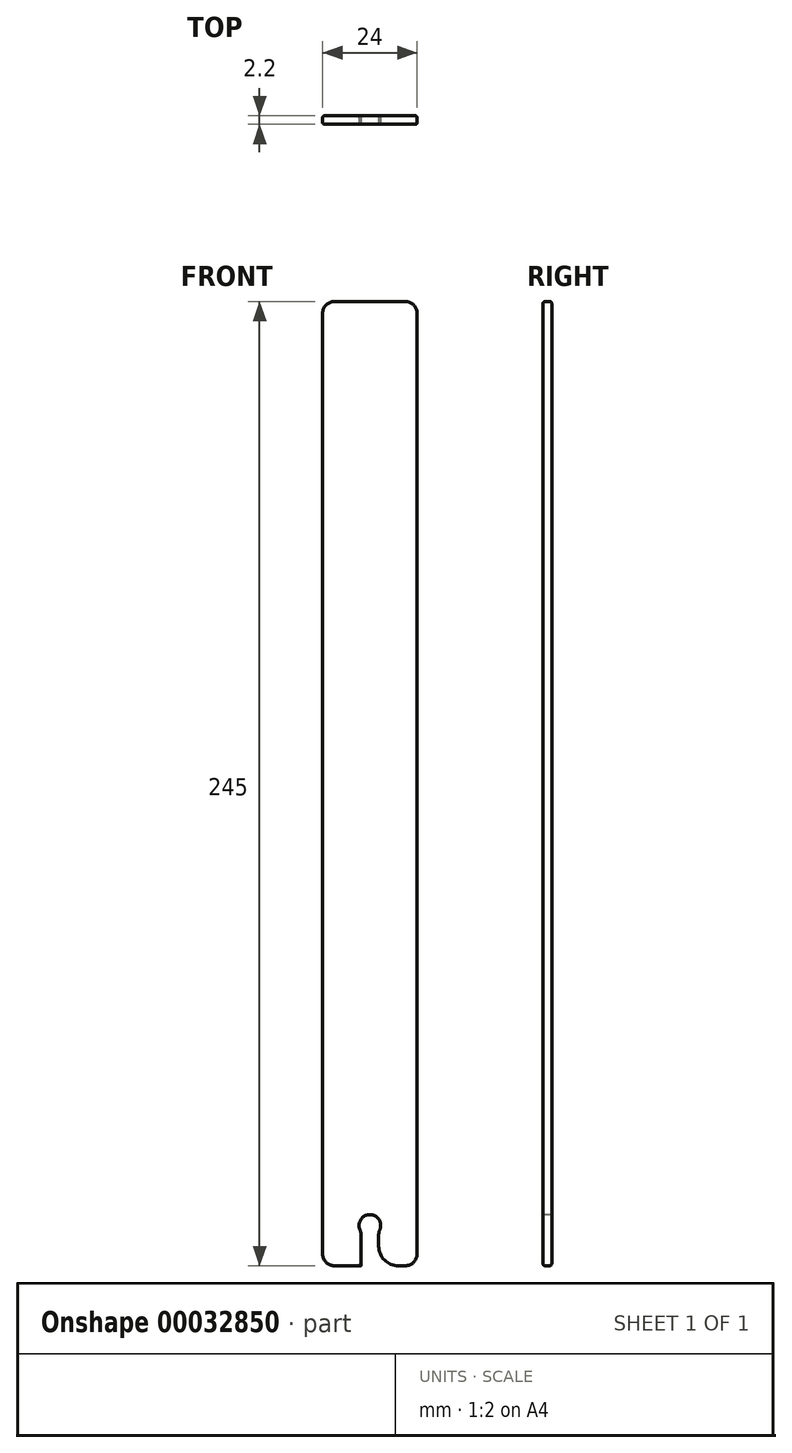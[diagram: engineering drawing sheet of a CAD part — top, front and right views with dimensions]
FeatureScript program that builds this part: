
annotation { "Feature Type Name" : "Feature", "Feature Type Description" : "" }
export const myFeature = defineFeature(function(context is Context, id is Id, definition is map)
    precondition{}
    {
        {
            var Q0;
            Q0=qCreatedBy(makeId("Top.planeOp"),FACE);
            var sketch = newSketch(context, id + "F0", { "sketchPlane" : qUnion([Q0])});
            skLineSegment(sketch, "E0.rect.bottom", {"start": v(12, 1.1) * mm, "end": v(-12, 1.1) * mm});
            skLineSegment(sketch, "E0.rect.top", {"start": v(12, -1.1) * mm, "end": v(-12, -1.1) * mm});
            skLineSegment(sketch, "E0.rect.left", {"start": v(12, 1.1) * mm, "end": v(12, -1.1) * mm});
            skLineSegment(sketch, "E0.rect.right", {"start": v(-12, 1.1) * mm, "end": v(-12, -1.1) * mm});
            skPoint(sketch, "E0.rect.middle", {"position": v(0, 0) * mm});
            skSolve(sketch);
        }
        {
            var Q0;
            Q0 = qSketchRegion(id + "F0", true);
            extrude(context, id + "F1", {"entities" : qUnion([Q0]), "depth" : 245 * mm});
        }
        {
            var Q0;
            Q0=qCreatedBy(makeId("Front.planeOp"),FACE);
            var sketch = newSketch(context, id + "F2", { "sketchPlane" : qUnion([Q0])});
            skArc(sketch, "E1", {"start": v(2.25, 8.67) * mm, "mid": v(0, 13) * mm, "end": v(-2.25, 8.67) * mm});
            skLineSegment(sketch, "E2", {"start": v(-2.25, 8.67) * mm, "end": v(-2.25, 0) * mm});
            skLineSegment(sketch, "E3.MirrorCS", {"start": v(2.25, 8.67) * mm, "end": v(2.25, 0) * mm});
            skPoint(sketch, "E4", {"position": v(0, 13) * mm});
            skLineSegment(sketch, "E5", {"start": v(-2.25, 0) * mm, "end": v(2.25, 0) * mm});
            skSolve(sketch);
        }
        {
            var Q0;
            Q0 = qSketchRegion(id + "F2", true);
            extrude(context, id + "F3", {"entities" : qUnion([Q0]), "operationType" : NewBodyOperationType.REMOVE, "endBound" : BoundingType.THROUGH_ALL, "oppositeDirection" : true, "depth" : 25 * mm, "hasSecondDirection" : true, "secondDirectionBound" : SecondDirectionBoundingType.THROUGH_ALL, "secondDirectionOppositeDirection" : false, "secondDirectionDepth" : 25 * mm});
        }
        {
            var Q0;
            Q0=makeQuery(id+"F3.boolean.opBoolean","COPY",EDGE,{"derivedFrom":makeQuery(id+"F3.opExtrude","SWEPT_EDGE",EDGE,{"disambiguationData":[OSD([sQuery(id+"F2.wireOp",EDGE,"E3.MirrorCS"),sQuery(id+"F2.wireOp",EDGE,"E5")])]})});
            var Q1;
            Q1=makeQuery(id+"F3.boolean.opBoolean","COPY",EDGE,{"derivedFrom":makeQuery(id+"F3.opExtrude","SWEPT_EDGE",EDGE,{"disambiguationData":[OSD([sQuery(id+"F2.wireOp",EDGE,"E2"),sQuery(id+"F2.wireOp",EDGE,"E5")])]})});
            fillet(context, id + "F4", {"entities" : qUnion([Q0, Q1]), "radius" : 5 * mm, "tangentPropagation" : true, "allowEdgeOverflow" : false});
        }
        {
            var Q0;
            Q0=makeQuery(id+"F3.boolean.opBoolean","COPY",EDGE,{"derivedFrom":makeQuery(id+"F3.opExtrude","SWEPT_EDGE",EDGE,{"disambiguationData":[OSD([sQuery(id+"F2.wireOp",EDGE,"E1"),sQuery(id+"F2.wireOp",EDGE,"E2")])]})});
            var Q1;
            Q1=makeQuery(id+"F3.boolean.opBoolean","COPY",EDGE,{"derivedFrom":makeQuery(id+"F3.opExtrude","SWEPT_EDGE",EDGE,{"disambiguationData":[OSD([sQuery(id+"F2.wireOp",EDGE,"E1"),sQuery(id+"F2.wireOp",EDGE,"E3.MirrorCS")])]})});
            fillet(context, id + "F5", {"entities" : qUnion([Q0, Q1]), "radius" : 3 * mm, "tangentPropagation" : true, "allowEdgeOverflow" : false});
        }
        {
            var Q0;
            Q0=makeQuery(id+"F1.opExtrude","CAP_EDGE",EDGE,{"disambiguationData":[OSD([sQuery(id+"F0.wireOp",EDGE,"E0.rect.left")])],"isStart":false});
            var Q1;
            Q1=makeQuery(id+"F1.opExtrude","CAP_EDGE",EDGE,{"disambiguationData":[OSD([sQuery(id+"F0.wireOp",EDGE,"E0.rect.right")])],"isStart":false});
            var Q2;
            Q2=makeQuery(id+"F1.opExtrude","CAP_EDGE",EDGE,{"disambiguationData":[OSD([sQuery(id+"F0.wireOp",EDGE,"E0.rect.right")])],"isStart":true});
            var Q3;
            Q3=makeQuery(id+"F1.opExtrude","CAP_EDGE",EDGE,{"disambiguationData":[OSD([sQuery(id+"F0.wireOp",EDGE,"E0.rect.left")])],"isStart":true});
            fillet(context, id + "F6", {"entities" : qUnion([Q0, Q1, Q2, Q3]), "radius" : 3 * mm, "tangentPropagation" : true, "allowEdgeOverflow" : false});
        }
        {
            var Q0;
            {var subQ0=sQuery(id+"F0.wireOp",EDGE,"E0.rect.bottom");Q0=makeQuery(id+"Fw8o0fSHUqNF145_1.boolean.opBoolean","SPLIT",EDGE,{"disambiguationData":[TD([makeQuery(id+"F1.opExtrude","SWEPT_FACE",FACE,{"disambiguationData":[OSD([subQ0])]}),makeQuery(id+"F1.opExtrude","CAP_FACE",FACE,{"disambiguationData":[OSD([subQ0,sQuery(id+"F0.wireOp",EDGE,"E0.rect.top"),sQuery(id+"F0.wireOp",EDGE,"E0.rect.left"),sQuery(id+"F0.wireOp",EDGE,"E0.rect.right")])],"isStart":false}),makeQuery(id+"Fw8o0fSHUqNF145_1.opExtrude","SWEPT_FACE",FACE,{"disambiguationData":[OSD([sQuery(id+"FbaGVTvyNiHfY6o_1.wireOp",EDGE,"9e5affed-078c-4892-bb57-0d6c6be92413")])]}),makeQuery(id+"Fw8o0fSHUqNF145_1.opExtrude","SWEPT_FACE",FACE,{"disambiguationData":[OSD([sQuery(id+"FbaGVTvyNiHfY6o_1.wireOp",EDGE,"08e1150b-f0ee-46df-a218-390a0e2899440.MirrorC")])]})])],"derivedFrom":makeQuery(id+"F1.opExtrude","CAP_EDGE",EDGE,{"disambiguationData":[OSD([subQ0])],"isStart":false})});}
            var Q1;
            {var subQ0=sQuery(id+"F0.wireOp",EDGE,"E0.rect.bottom");var subQ1=makeQuery(id+"F1.opExtrude","SWEPT_FACE",FACE,{"disambiguationData":[OSD([subQ0])]});var subQ2=makeQuery(id+"Fw8o0fSHUqNF145_1.opExtrude","SWEPT_FACE",FACE,{"disambiguationData":[OSD([sQuery(id+"FbaGVTvyNiHfY6o_1.wireOp",EDGE,"9e5affed-078c-4892-bb57-0d6c6be92413")])]});var subQ3=sQuery(id+"F0.wireOp",EDGE,"E0.rect.top");var subQ4=sQuery(id+"F0.wireOp",EDGE,"E0.rect.left");var subQ5=sQuery(id+"F0.wireOp",EDGE,"E0.rect.right");var subQ6=makeQuery(id+"F1.opExtrude","CAP_FACE",FACE,{"disambiguationData":[OSD([subQ0,subQ3,subQ4,subQ5])],"isStart":false});var subQ7=makeQuery(id+"F1.opExtrude","CAP_FACE",FACE,{"disambiguationData":[OSD([subQ0,subQ3,subQ4,subQ5])],"isStart":true});var subQ8=makeQuery(id+"Fw8o0fSHUqNF145_1.opExtrude","SWEPT_FACE",FACE,{"disambiguationData":[OSD([sQuery(id+"FbaGVTvyNiHfY6o_1.wireOp",EDGE,"08e1150b-f0ee-46df-a218-390a0e2899440.MirrorC")])]});Q1=makeQuery(id+"F3.boolean.opBoolean","INTERSECT",EDGE,{"derivedFrom":[makeQuery(id+"FPPC7eTGVXrOg84_1.boolean.opBoolean","MERGE",FACE,{"derivedFrom":[makeQuery(id+"Fw8o0fSHUqNF145_1.boolean.opBoolean","SPLIT",FACE,{"disambiguationData":[TD([subQ7,subQ6,makeQuery(id+"Fw8o0fSHUqNF145_1.opExtrude","SWEPT_FACE",FACE,{"disambiguationData":[OSD([sQuery(id+"FbaGVTvyNiHfY6o_1.wireOp",EDGE,"c1bc32d7-144e-444e-9ce3-39f3e85331c1")])]}),subQ2])],"derivedFrom":subQ1}),makeQuery(id+"Fw8o0fSHUqNF145_1.boolean.opBoolean","SPLIT",FACE,{"disambiguationData":[TD([subQ7,subQ6,subQ2,subQ8])],"derivedFrom":subQ1}),makeQuery(id+"Fw8o0fSHUqNF145_1.boolean.opBoolean","SPLIT",FACE,{"disambiguationData":[TD([subQ7,subQ6,subQ8,makeQuery(id+"Fw8o0fSHUqNF145_1.opExtrude","SWEPT_FACE",FACE,{"disambiguationData":[OSD([sQuery(id+"FbaGVTvyNiHfY6o_1.wireOp",EDGE,"d71e21d5-955b-49d5-8a50-ac33ae09a8a30.MirrorC")])]})])],"derivedFrom":subQ1}),makeQuery(id+"FPPC7eTGVXrOg84_1.opExtrude","SWEPT_FACE",FACE,{"disambiguationData":[OSD([sQuery(id+"FNljt0qgbT6XEaA_1.wireOp",EDGE,"6ea7042a-b0b0-46e1-8681-a8487cb0b644.bottom")])]})]}),makeQuery(id+"F3.opExtrude","SWEPT_FACE",FACE,{"disambiguationData":[OSD([sQuery(id+"F2.wireOp",EDGE,"E1")])]})]});}
            var Q2;
            {var subQ0=sQuery(id+"F0.wireOp",EDGE,"E0.rect.top");var subQ1=sQuery(id+"F0.wireOp",EDGE,"E0.rect.right");Q2=makeQuery(id+"Fw8o0fSHUqNF145_1.boolean.opBoolean","SPLIT",EDGE,{"disambiguationData":[TD([makeQuery(id+"F1.opExtrude","CAP_FACE",FACE,{"disambiguationData":[OSD([sQuery(id+"F0.wireOp",EDGE,"E0.rect.bottom"),subQ0,sQuery(id+"F0.wireOp",EDGE,"E0.rect.left"),subQ1])],"isStart":true}),makeQuery(id+"F1.opExtrude","SWEPT_FACE",FACE,{"disambiguationData":[OSD([subQ0])]}),makeQuery(id+"F1.opExtrude","SWEPT_FACE",FACE,{"disambiguationData":[OSD([subQ1])]}),makeQuery(id+"Fw8o0fSHUqNF145_1.opExtrude","SWEPT_FACE",FACE,{"disambiguationData":[OSD([sQuery(id+"FbaGVTvyNiHfY6o_1.wireOp",EDGE,"dc26be96-5341-4068-be16-d0b10b79afae0.MirrorC")])]})])],"derivedFrom":makeQuery(id+"F1.opExtrude","CAP_EDGE",EDGE,{"disambiguationData":[OSD([subQ0])],"isStart":true})});}
            var Q3;
            {var subQ0=sQuery(id+"F0.wireOp",EDGE,"E0.rect.top");Q3=makeQuery(id+"Fw8o0fSHUqNF145_1.boolean.opBoolean","SPLIT",EDGE,{"disambiguationData":[TD([makeQuery(id+"F1.opExtrude","CAP_FACE",FACE,{"disambiguationData":[OSD([sQuery(id+"F0.wireOp",EDGE,"E0.rect.bottom"),subQ0,sQuery(id+"F0.wireOp",EDGE,"E0.rect.left"),sQuery(id+"F0.wireOp",EDGE,"E0.rect.right")])],"isStart":false}),makeQuery(id+"F1.opExtrude","SWEPT_FACE",FACE,{"disambiguationData":[OSD([subQ0])]}),makeQuery(id+"Fw8o0fSHUqNF145_1.opExtrude","SWEPT_FACE",FACE,{"disambiguationData":[OSD([sQuery(id+"FbaGVTvyNiHfY6o_1.wireOp",EDGE,"1b47d79e-034d-4dfa-9253-97eb4d77fb7f")])]}),makeQuery(id+"Fw8o0fSHUqNF145_1.opExtrude","SWEPT_FACE",FACE,{"disambiguationData":[OSD([sQuery(id+"FbaGVTvyNiHfY6o_1.wireOp",EDGE,"f59acf01-e540-4f04-88a9-ca8e575c952f")])]})])],"derivedFrom":makeQuery(id+"F1.opExtrude","CAP_EDGE",EDGE,{"disambiguationData":[OSD([subQ0])],"isStart":false})});}
            fillet(context, id + "F7", {"entities" : qUnion([Q0, Q1, Q2, Q3]), "radius" : 0.5 * mm, "tangentPropagation" : true, "allowEdgeOverflow" : false});
        }
    });
